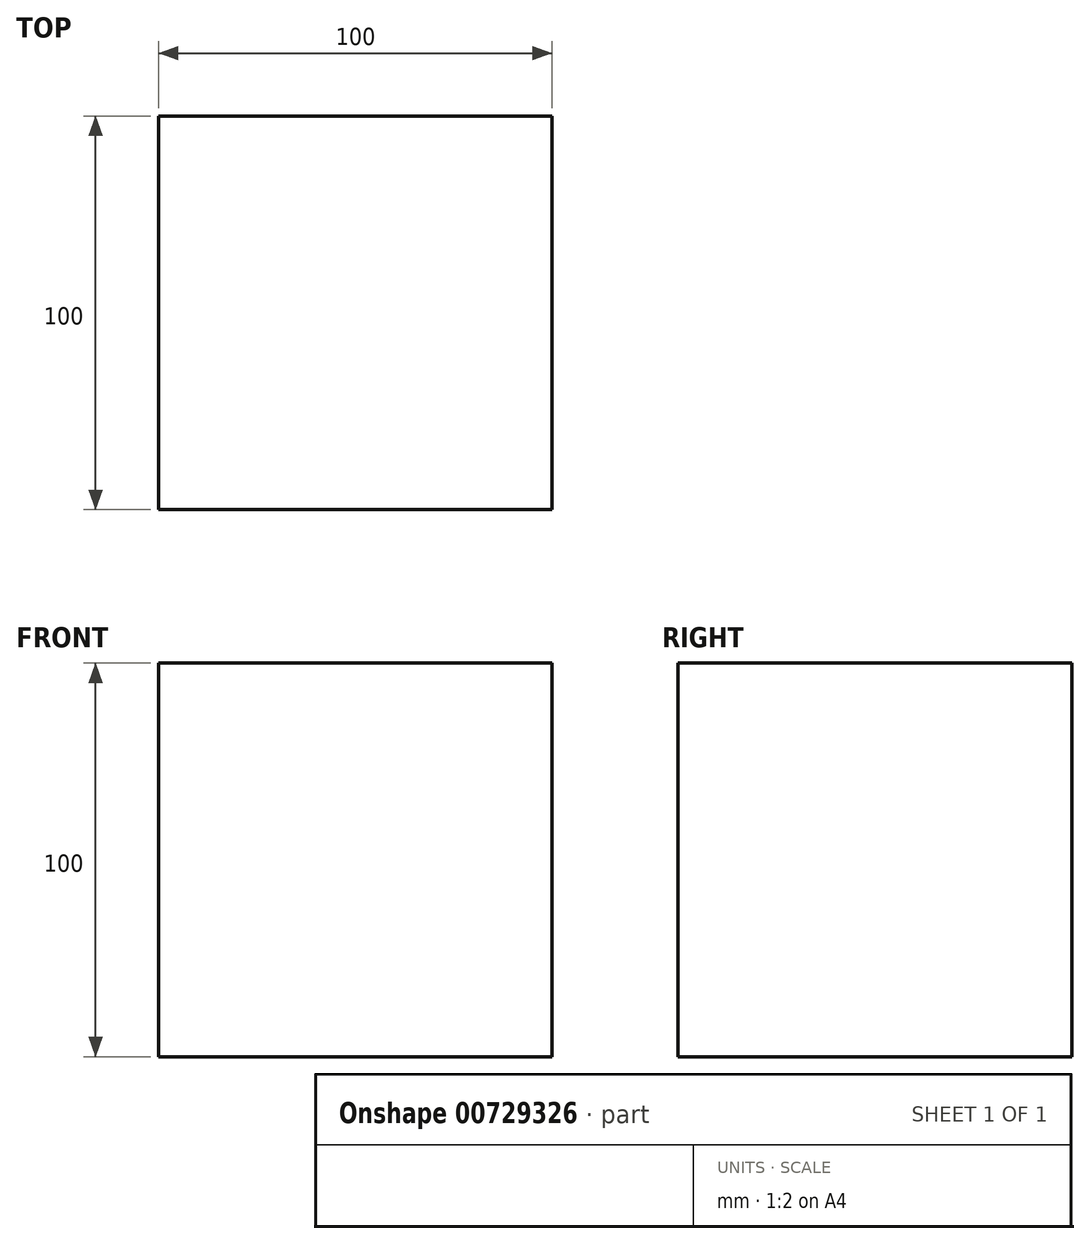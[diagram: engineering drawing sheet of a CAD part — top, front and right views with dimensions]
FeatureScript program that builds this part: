
annotation { "Feature Type Name" : "Feature", "Feature Type Description" : "" }
export const myFeature = defineFeature(function(context is Context, id is Id, definition is map)
    precondition{}
    {
        {
            var Q0;
            Q0=qCreatedBy(makeId("Top.planeOp"),FACE);
            var sketch = newSketch(context, id + "F0", { "sketchPlane" : qUnion([Q0])});
            skLineSegment(sketch, "E0.bottom", {"start": v(-50, 50) * mm, "end": v(50, 50) * mm});
            skLineSegment(sketch, "E0.top", {"start": v(-50, -50) * mm, "end": v(50, -50) * mm});
            skLineSegment(sketch, "E0.left", {"start": v(-50, 50) * mm, "end": v(-50, -50) * mm});
            skLineSegment(sketch, "E0.right", {"start": v(50, 50) * mm, "end": v(50, -50) * mm});
            skPoint(sketch, "E0.middle", {"position": v(0, 0) * mm});
            skSolve(sketch);
        }
        {
            var Q0;
            Q0=makeQuery(id+"F0.imprint","IMPRINT",FACE,{"disambiguationData":[TD([[makeQuery(id+"F0.imprint","IMPRINT",EDGE,{"derivedFrom":sQuery(id+"F0.wireOp",EDGE,"E0.bottom")}),-1.0]])]});
            extrude(context, id + "F1", {"entities" : qUnion([Q0]), "endBound" : BoundingType.SYMMETRIC, "depth" : 100 * mm, "offsetDistance" : 25 * mm});
        }
    });
